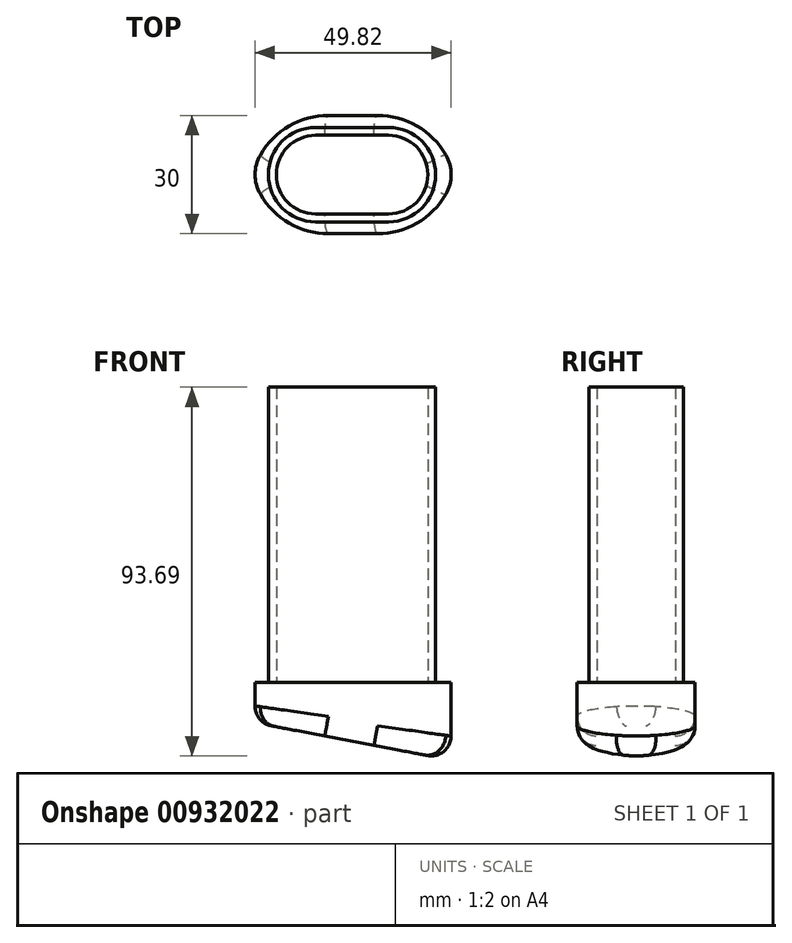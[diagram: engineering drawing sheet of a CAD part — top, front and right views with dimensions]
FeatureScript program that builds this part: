
annotation { "Feature Type Name" : "Feature", "Feature Type Description" : "" }
export const myFeature = defineFeature(function(context is Context, id is Id, definition is map)
    precondition{}
    {
        {
            var Q0;
            Q0=qCreatedBy(makeId("Top.planeOp"),FACE);
            var sketch = newSketch(context, id + "F0", { "sketchPlane" : qUnion([Q0])});
            skArc(sketch, "E0", {"start": v(-30.76, 10) * mm, "mid": v(-40.76, 0) * mm, "end": v(-30.76, -10) * mm});
            skArc(sketch, "E1", {"start": v(-12.26, -10) * mm, "mid": v(-2.26, 0) * mm, "end": v(-12.26, 10) * mm});
            skLineSegment(sketch, "E2", {"start": v(-30.76, -10) * mm, "end": v(-12.26, -10) * mm});
            skLineSegment(sketch, "E3", {"start": v(-30.76, 10) * mm, "end": v(-12.26, 10) * mm});
            skCircle(sketch, "E4", {"center": v(-30.76, 0) * mm, "radius": 12 * mm});
            skCircle(sketch, "E5", {"center": v(-12.26, 0) * mm, "radius": 12 * mm});
            skLineSegment(sketch, "E6", {"start": v(-30.76, 12) * mm, "end": v(-12.26, 12) * mm});
            skLineSegment(sketch, "E7", {"start": v(-30.76, -12) * mm, "end": v(-12.26, -12) * mm});
            skSolve(sketch);
        }
        {
            var Q0;
            Q0 = qSketchRegion(id + "F0", true);
            extrude(context, id + "F1", {"entities" : qUnion([Q0]), "depth" : 75 * mm, "offsetDistance" : 25.4 * mm});
        }
        {
            var Q0;
            Q0=qCreatedBy(makeId("Front.planeOp"),FACE);
            var sketch = newSketch(context, id + "F2", { "sketchPlane" : qUnion([Q0])});
            skLineSegment(sketch, "E8", {"start": v(5, 0) * mm, "end": v(5, -20) * mm});
            skLineSegment(sketch, "E9", {"start": v(5, -20) * mm, "end": v(-47.5, -10) * mm});
            skLineSegment(sketch, "E10", {"start": v(-47.5, -10) * mm, "end": v(-47.5, 0) * mm});
            skLineSegment(sketch, "E11", {"start": v(5, 0) * mm, "end": v(-47.5, 0) * mm});
            skSolve(sketch);
        }
        {
            var Q0;
            Q0 = qSketchRegion(id + "F2", true);
            extrude(context, id + "F3", {"entities" : qUnion([Q0]), "operationType" : NewBodyOperationType.ADD, "depth" : 30 * mm, "offsetDistance" : 25.4 * mm, "symmetric" : true});
        }
        {
            var Q0;
            Q0=makeQuery(id+"F3.opExtrude","CAP_EDGE",EDGE,{"disambiguationData":[OSD([sQuery(id+"F2.wireOp",EDGE,"E8")])],"isStart":true});
            var Q1;
            Q1=makeQuery(id+"F3.opExtrude","CAP_EDGE",EDGE,{"disambiguationData":[OSD([sQuery(id+"F2.wireOp",EDGE,"E8")])],"isStart":false});
            var Q2;
            Q2=makeQuery(id+"F3.opExtrude","CAP_EDGE",EDGE,{"disambiguationData":[OSD([sQuery(id+"F2.wireOp",EDGE,"E10")])],"isStart":false});
            var Q3;
            Q3=makeQuery(id+"F3.opExtrude","CAP_EDGE",EDGE,{"disambiguationData":[OSD([sQuery(id+"F2.wireOp",EDGE,"E10")])],"isStart":true});
            fillet(context, id + "F4", {"entities" : qUnion([Q0, Q1, Q2, Q3]), "radius" : 20 * mm, "tangentPropagation" : true, "allowEdgeOverflow" : false});
        }
        {
            var Q0;
            {var subQ0=sQuery(id+"F2.wireOp",EDGE,"E10");Q0=makeQuery(id+"F4.opFillet","BLEND_EDGE",EDGE,{"blendedFrom":[makeQuery(id+"F3.opExtrude","CAP_EDGE",EDGE,{"disambiguationData":[OSD([subQ0])],"isStart":true}),makeQuery(id+"F3.opExtrude","CAP_EDGE",EDGE,{"disambiguationData":[OSD([subQ0])],"isStart":false})],"blendedInto":[]});}
            var Q1;
            {var subQ0=sQuery(id+"F2.wireOp",EDGE,"E8");Q1=makeQuery(id+"F4.opFillet","BLEND_EDGE",EDGE,{"blendedFrom":[makeQuery(id+"F3.opExtrude","CAP_EDGE",EDGE,{"disambiguationData":[OSD([subQ0])],"isStart":true}),makeQuery(id+"F3.opExtrude","CAP_EDGE",EDGE,{"disambiguationData":[OSD([subQ0])],"isStart":false})],"blendedInto":[]});}
            fillet(context, id + "F5", {"entities" : qUnion([Q0, Q1]), "radius" : 10 * mm, "tangentPropagation" : true, "allowEdgeOverflow" : false});
        }
        {
            var Q0;
            Q0=makeQuery(id+"F3.opExtrude","CAP_EDGE",EDGE,{"disambiguationData":[OSD([sQuery(id+"F2.wireOp",EDGE,"E9")])],"isStart":false});
            fillet(context, id + "F6", {"entities" : qUnion([Q0]), "radius" : 5.08 * mm, "tangentPropagation" : true, "allowEdgeOverflow" : false});
        }
    });
